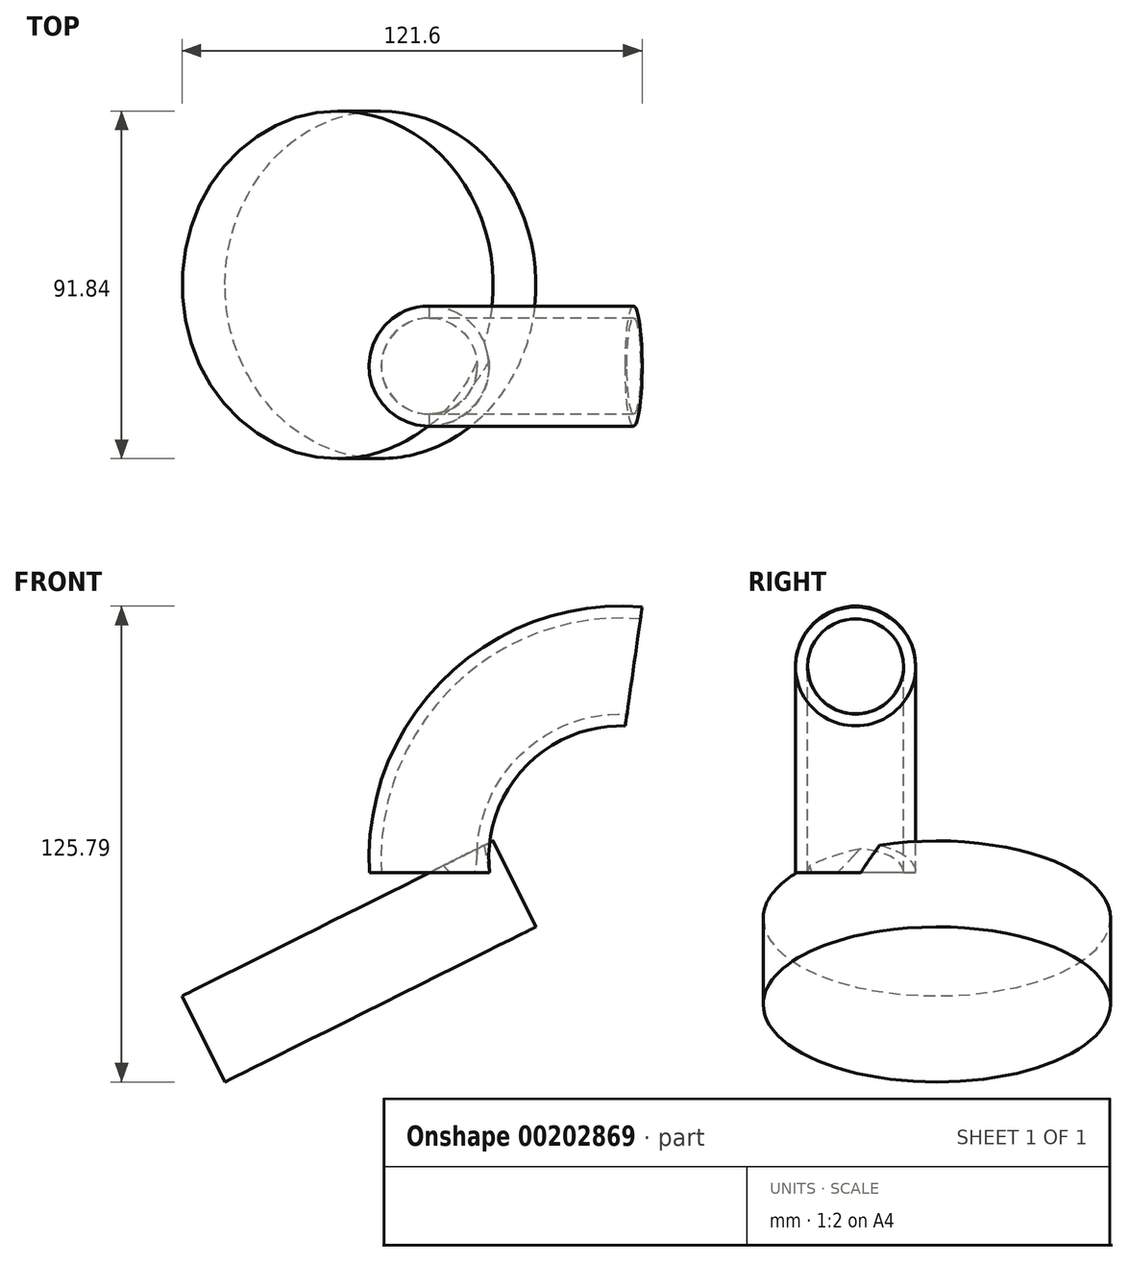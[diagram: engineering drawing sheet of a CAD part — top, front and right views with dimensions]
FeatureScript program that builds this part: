
annotation { "Feature Type Name" : "Feature", "Feature Type Description" : "" }
export const myFeature = defineFeature(function(context is Context, id is Id, definition is map)
    precondition{}
    {
        {
            var Q0;
            Q0=qCreatedBy(makeId("Top.planeOp"),FACE);
            var sketch = newSketch(context, id + "F0", { "sketchPlane" : qUnion([Q0])});
            skCircle(sketch, "E0", {"center": v(0, 0) * mm, "radius": 12.7 * mm});
            skCircle(sketch, "E1", {"center": v(0, 0) * mm, "radius": 15.88 * mm});
            skSolve(sketch);
        }
        {
            var Q0;
            Q0=qCreatedBy(makeId("Front.planeOp"),FACE);
            var sketch = newSketch(context, id + "F1", { "sketchPlane" : qUnion([Q0])});
            skArc(sketch, "E2", {"start": v(54, 54.5) * mm, "mid": v(14.56, 39.57) * mm, "end": v(0, 0) * mm});
            skSolve(sketch);
        }
        {
            var Q0;
            Q0=makeQuery(id+"F0.imprint","IMPRINT",FACE,{"disambiguationData":[TD([[makeQuery(id+"F0.imprint","IMPRINT",EDGE,{"derivedFrom":sQuery(id+"F0.wireOp",EDGE,"E0")}),-1.0]])]});
            var Q1;
            Q1=sQuery(id+"F1.wireOp",EDGE,"E2");
            sweep(context, id + "F2", {"profiles" : qUnion([Q0]), "path" : qUnion([Q1])});
        }
        {
            var Q0;
            Q0=qCreatedBy(makeId("Front.planeOp"),FACE);
            var sketch = newSketch(context, id + "F3", { "sketchPlane" : qUnion([Q0])});
            skLineSegment(sketch, "E3", {"start": v(0, 0) * mm, "end": v(-49.1, 0) * mm});
            skLineSegment(sketch, "E4", {"start": v(-49.1, 0) * mm, "end": v(-49.1, -24.48) * mm});
            skLineSegment(sketch, "E5", {"start": v(-49.1, -24.48) * mm, "end": v(0, 0) * mm});
            skSolve(sketch);
        }
        {
            var Q0;
            Q0=qCreatedBy(makeId("Top.planeOp"),FACE);
            var sketch = newSketch(context, id + "F4", { "sketchPlane" : qUnion([Q0])});
            skPoint(sketch, "E6", {"position": v(0, 41.97) * mm});
            skSolve(sketch);
        }
        {
            var Q0;
            Q0=sQuery(id+"F3.wireOp",VERTEX,"E5.end");
            var Q1;
            Q1=sQuery(id+"F4.wireOp",VERTEX,"E6");
            var Q2;
            Q2=sQuery(id+"F3.wireOp",VERTEX,"E5.start");
            cPlane(context, id + "F5", {"entities" : qUnion([Q0, Q1, Q2]), "cplaneType" : CPlaneType.THREE_POINT, "offset" : 25.4 * mm, "width" : 152.4 * mm, "height" : 152.4 * mm});
        }
        {
            var Q0;
            Q0=qCreatedBy(id+"F5.planeOp",FACE);
            var sketch = newSketch(context, id + "F6", { "sketchPlane" : qUnion([Q0])});
            skCircle(sketch, "E7", {"center": v(-27.13, -21.47) * mm, "radius": 45.92 * mm});
            skSolve(sketch);
        }
        {
            var Q0;
            Q0 = qSketchRegion(id + "F6", true);
            extrude(context, id + "F7", {"entities" : qUnion([Q0]), "operationType" : NewBodyOperationType.ADD, "depth" : 25.4 * mm});
        }
    });
